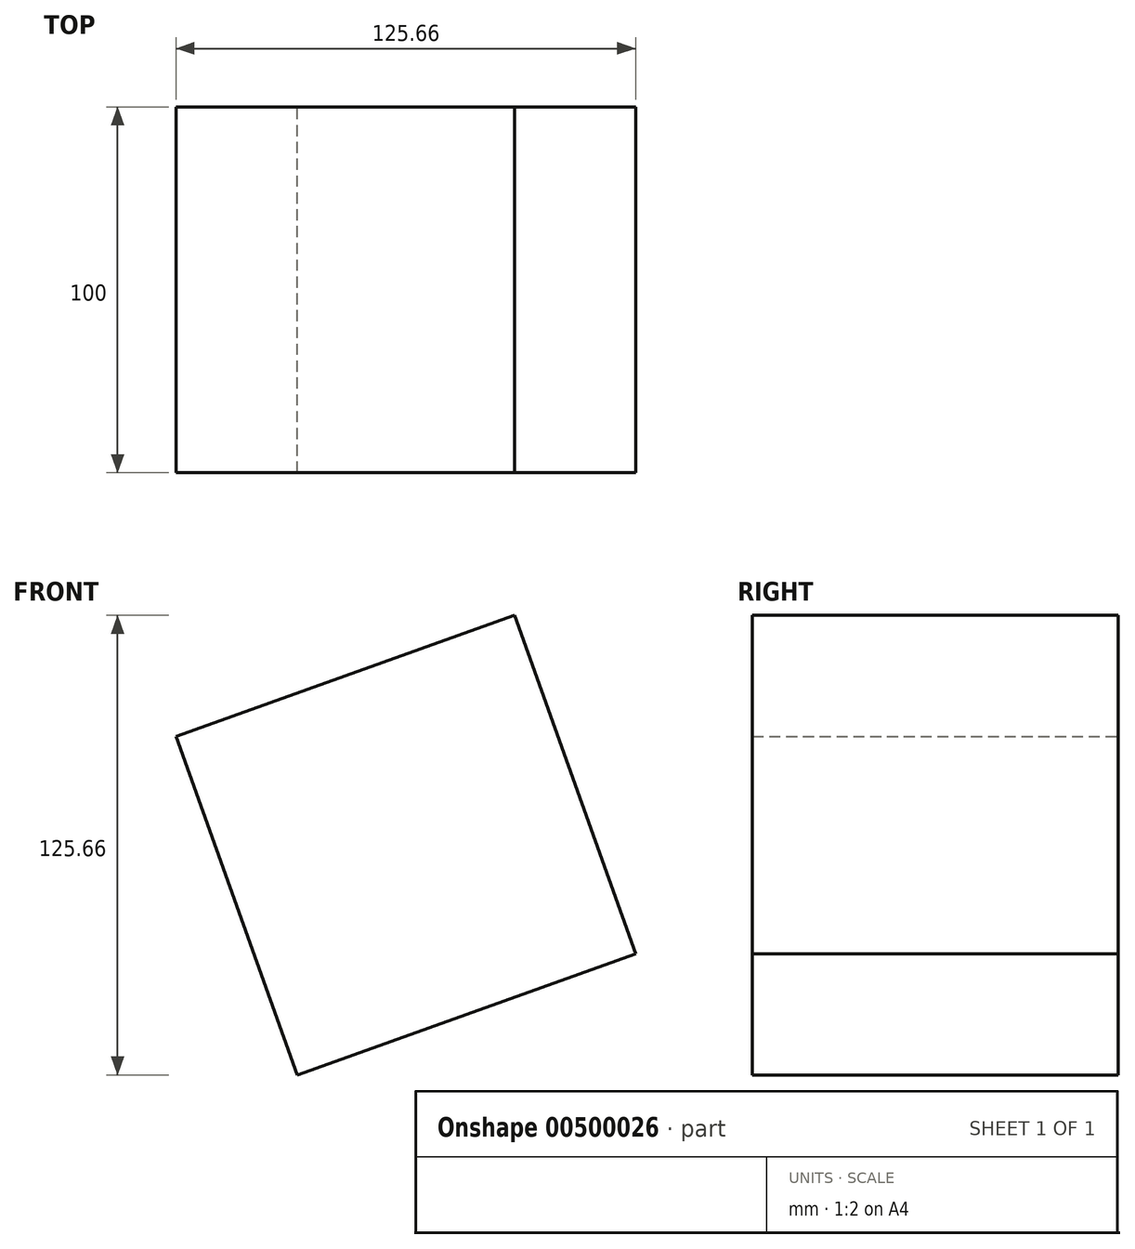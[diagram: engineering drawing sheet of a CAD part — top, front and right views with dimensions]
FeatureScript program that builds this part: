
annotation { "Feature Type Name" : "Feature", "Feature Type Description" : "" }
export const myFeature = defineFeature(function(context is Context, id is Id, definition is map)
    precondition{}
    {
        {
            var Q0;
            Q0=qCreatedBy(makeId("Front.planeOp"),FACE);
            var sketch = newSketch(context, id + "F0", { "sketchPlane" : qUnion([Q0])});
            skCircle(sketch, "E0.cCircle", {"center": v(0, 0) * mm, "radius": 69.5 * mm, "construction": true});
            skLineSegment(sketch, "E0.0", {"start": v(-62.83, 29.7) * mm, "end": v(29.7, 62.83) * mm});
            skLineSegment(sketch, "E0.1", {"start": v(29.7, 62.83) * mm, "end": v(62.83, -29.7) * mm});
            skLineSegment(sketch, "E0.2", {"start": v(62.83, -29.7) * mm, "end": v(-29.7, -62.83) * mm});
            skLineSegment(sketch, "E0.3", {"start": v(-29.7, -62.83) * mm, "end": v(-62.83, 29.7) * mm});
            skSolve(sketch);
        }
        {
            var Q0;
            Q0=makeQuery(id+"F0.imprint","IMPRINT",FACE,{"disambiguationData":[TD([[makeQuery(id+"F0.imprint","IMPRINT",EDGE,{"derivedFrom":sQuery(id+"F0.wireOp",EDGE,"E0.0")}),-1.0]])]});
            extrude(context, id + "F1", {"entities" : qUnion([Q0]), "endBound" : BoundingType.SYMMETRIC, "depth" : 100 * mm});
        }
    });
